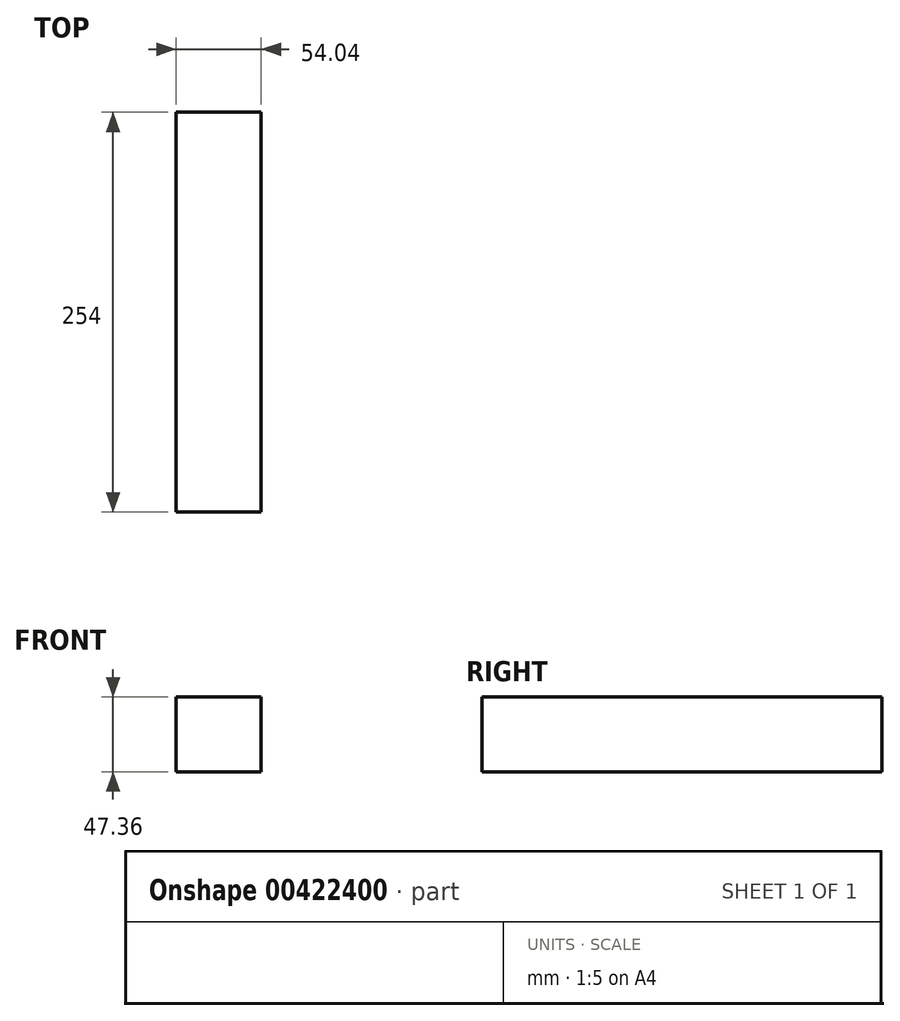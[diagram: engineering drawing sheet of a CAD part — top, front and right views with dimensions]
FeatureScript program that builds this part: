
annotation { "Feature Type Name" : "Feature", "Feature Type Description" : "" }
export const myFeature = defineFeature(function(context is Context, id is Id, definition is map)
    precondition{}
    {
        {
            var Q0;
            Q0=qCreatedBy(makeId("Front.planeOp"),FACE);
            var sketch = newSketch(context, id + "F0", { "sketchPlane" : qUnion([Q0])});
            skLineSegment(sketch, "E0.bottom", {"start": v(0, 0) * mm, "end": v(-54.04, 0) * mm});
            skLineSegment(sketch, "E0.top", {"start": v(0, 47.36) * mm, "end": v(-54.04, 47.36) * mm});
            skLineSegment(sketch, "E0.left", {"start": v(0, 0) * mm, "end": v(0, 47.36) * mm});
            skLineSegment(sketch, "E0.right", {"start": v(-54.04, 0) * mm, "end": v(-54.04, 47.36) * mm});
            skSolve(sketch);
        }
        {
            var Q0;
            Q0 = qSketchRegion(id + "F0", true);
            extrude(context, id + "F1", {"entities" : qUnion([Q0]), "depth" : 254 * mm});
        }
    });
